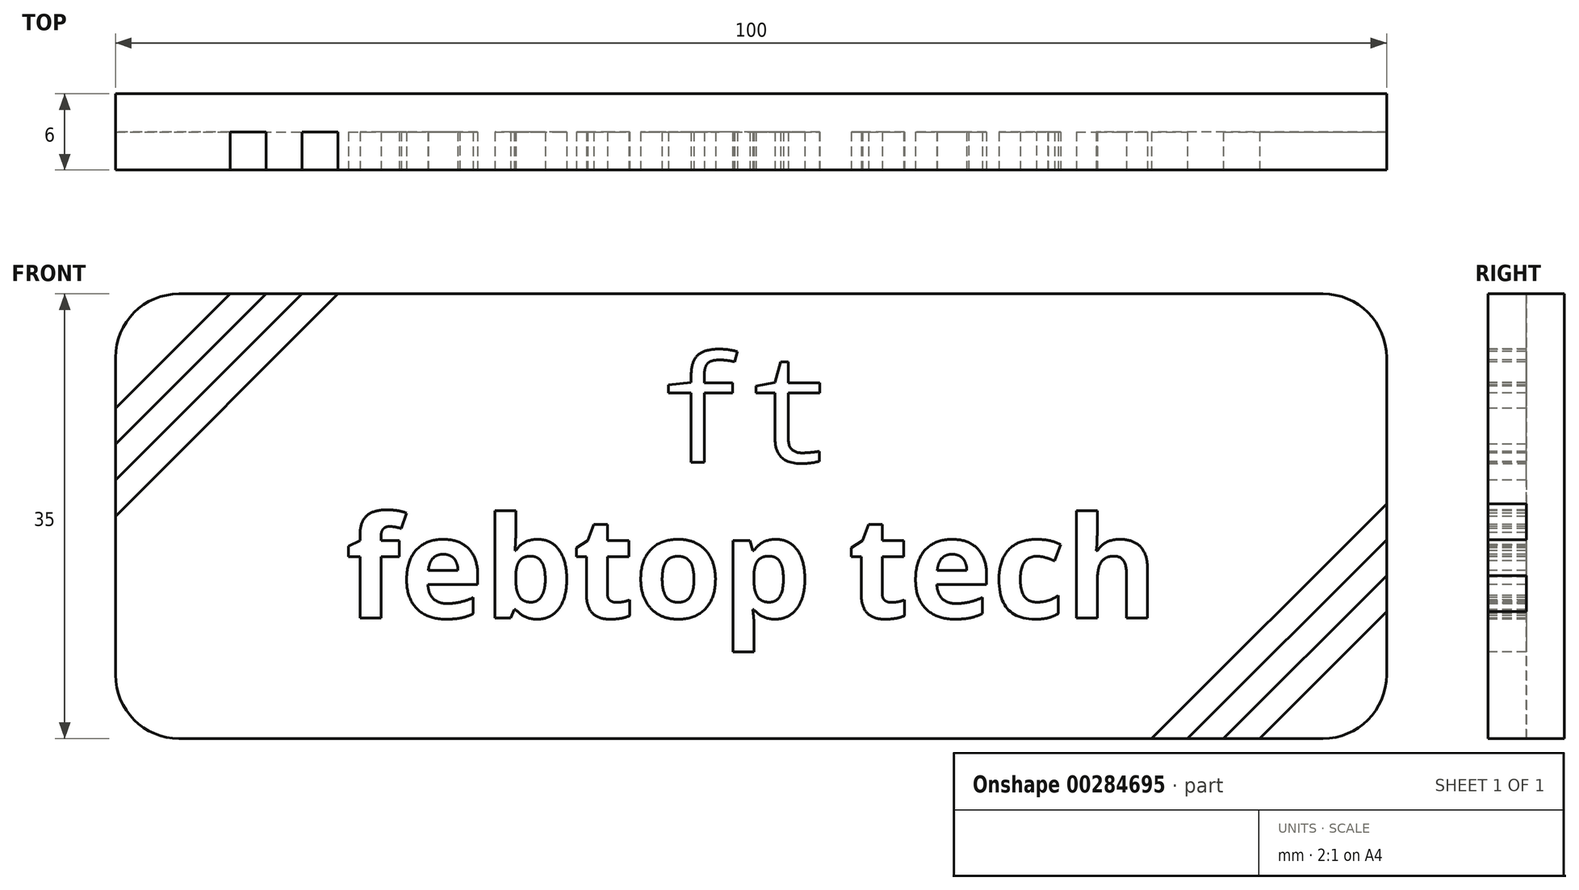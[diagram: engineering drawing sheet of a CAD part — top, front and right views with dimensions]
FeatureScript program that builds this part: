
annotation { "Feature Type Name" : "Feature", "Feature Type Description" : "" }
export const myFeature = defineFeature(function(context is Context, id is Id, definition is map)
    precondition{}
    {
        {
            var Q0;
            Q0=qCreatedBy(makeId("Front.planeOp"),FACE);
            var sketch = newSketch(context, id + "F0", { "sketchPlane" : qUnion([Q0])});
            skLineSegment(sketch, "E0.bottom", {"start": v(-45, 17.5) * mm, "end": v(45, 17.5) * mm});
            skLineSegment(sketch, "E0.top", {"start": v(-45, -17.5) * mm, "end": v(45, -17.5) * mm});
            skLineSegment(sketch, "E0.left", {"start": v(-50, 12.5) * mm, "end": v(-50, -12.5) * mm});
            skLineSegment(sketch, "E0.right", {"start": v(50, 12.5) * mm, "end": v(50, -12.5) * mm});
            skPoint(sketch, "E1.visualSharp", {"position": v(-50, 17.5) * mm});
            skArc(sketch, "E1.filletArc", {"start": v(-45, 17.5) * mm, "mid": v(-48.54, 16.04) * mm, "end": v(-50, 12.5) * mm});
            skPoint(sketch, "E2.visualSharp", {"position": v(-50, -17.5) * mm});
            skArc(sketch, "E2.filletArc", {"start": v(-50, -12.5) * mm, "mid": v(-48.54, -16.04) * mm, "end": v(-45, -17.5) * mm});
            skPoint(sketch, "E3.visualSharp", {"position": v(50, -17.5) * mm});
            skArc(sketch, "E3.filletArc", {"start": v(45, -17.5) * mm, "mid": v(48.54, -16.04) * mm, "end": v(50, -12.5) * mm});
            skPoint(sketch, "E4.visualSharp", {"position": v(50, 17.5) * mm});
            skArc(sketch, "E4.filletArc", {"start": v(50, 12.5) * mm, "mid": v(48.54, 16.04) * mm, "end": v(45, 17.5) * mm});
            skSolve(sketch);
        }
        {
            var Q0;
            Q0=makeQuery(id+"F0.imprint","IMPRINT",FACE,{"disambiguationData":[TD([[makeQuery(id+"F0.imprint","IMPRINT",EDGE,{"derivedFrom":sQuery(id+"F0.wireOp",EDGE,"E0.bottom")}),-1.0]])]});
            extrude(context, id + "F1", {"entities" : qUnion([Q0]), "depth" : 6 * mm});
        }
        {
            var Q0;
            Q0=makeQuery(id+"F1.opExtrude","CAP_FACE",FACE,{"disambiguationData":[OSD([sQuery(id+"F0.wireOp",EDGE,"E0.bottom"),sQuery(id+"F0.wireOp",EDGE,"E0.top"),sQuery(id+"F0.wireOp",EDGE,"E0.left"),sQuery(id+"F0.wireOp",EDGE,"E0.right"),sQuery(id+"F0.wireOp",EDGE,"E1.filletArc"),sQuery(id+"F0.wireOp",EDGE,"E2.filletArc"),sQuery(id+"F0.wireOp",EDGE,"E3.filletArc"),sQuery(id+"F0.wireOp",EDGE,"E4.filletArc")])],"isStart":false});
            var sketch = newSketch(context, id + "F2", { "sketchPlane" : qUnion([Q0])});
            skLineSegment(sketch, "E5", {"start": v(-40.99, 17.5) * mm, "end": v(-50, 8.49) * mm});
            skLineSegment(sketch, "E6", {"start": v(-50, 8.49) * mm, "end": v(-50, 5.66) * mm});
            skLineSegment(sketch, "E7", {"start": v(-50, 5.66) * mm, "end": v(-38.16, 17.5) * mm});
            skLineSegment(sketch, "E8", {"start": v(-50, 2.83) * mm, "end": v(-35.33, 17.5) * mm});
            skLineSegment(sketch, "E9", {"start": v(-50, 0) * mm, "end": v(-32.5, 17.5) * mm});
            skLineSegment(sketch, "E10", {"start": v(40, -17.5) * mm, "end": v(50, -7.5) * mm});
            skLineSegment(sketch, "E11", {"start": v(37.17, -17.5) * mm, "end": v(50, -4.67) * mm});
            skLineSegment(sketch, "E12", {"start": v(50, -1.84) * mm, "end": v(34.34, -17.5) * mm});
            skLineSegment(sketch, "E13", {"start": v(50, 0.99) * mm, "end": v(31.51, -17.5) * mm});
            skSolve(sketch);
        }
        {
            var Q0;
            {var subQ0=sQuery(id+"F2.wireOp",EDGE,"E5");Q0=makeQuery(id+"F2.imprint","IMPRINT",FACE,{"disambiguationData":[TD([[makeQuery(id+"F2.imprint","IMPRINT",EDGE,{"derivedFrom":subQ0}),1.0]])]});}
            var Q1;
            {var subQ0=sQuery(id+"F2.wireOp",EDGE,"E8");Q1=makeQuery(id+"F2.imprint","IMPRINT",FACE,{"disambiguationData":[TD([[makeQuery(id+"F2.imprint","IMPRINT",EDGE,{"derivedFrom":subQ0}),-1.0]])]});}
            var Q2;
            {var subQ0=sQuery(id+"F2.wireOp",EDGE,"E12");Q2=makeQuery(id+"F2.imprint","IMPRINT",FACE,{"disambiguationData":[TD([[makeQuery(id+"F2.imprint","IMPRINT",EDGE,{"derivedFrom":subQ0}),-1.0]])]});}
            var Q3;
            {var subQ0=sQuery(id+"F2.wireOp",EDGE,"E10");Q3=makeQuery(id+"F2.imprint","IMPRINT",FACE,{"disambiguationData":[TD([[makeQuery(id+"F2.imprint","IMPRINT",EDGE,{"derivedFrom":subQ0}),1.0]])]});}
            extrude(context, id + "F3", {"entities" : qUnion([Q0, Q1, Q2, Q3]), "operationType" : NewBodyOperationType.REMOVE, "oppositeDirection" : true, "depth" : 3 * mm});
        }
        {
            var Q0;
            {var subQ0=sQuery(id+"F0.wireOp",EDGE,"E0.left");var subQ1=sQuery(id+"F0.wireOp",EDGE,"E0.top");var subQ2=sQuery(id+"F0.wireOp",EDGE,"E0.right");var subQ3=sQuery(id+"F0.wireOp",EDGE,"E0.bottom");var subQ4=sQuery(id+"F0.wireOp",EDGE,"E2.filletArc");var subQ5=sQuery(id+"F0.wireOp",EDGE,"E4.filletArc");Q0=makeQuery(id+"F3.boolean.opBoolean","SPLIT",FACE,{"disambiguationData":[TD([makeQuery(id+"F1.opExtrude","SWEPT_FACE",FACE,{"disambiguationData":[OSD([subQ4])]})])],"derivedFrom":makeQuery(id+"F1.opExtrude","CAP_FACE",FACE,{"disambiguationData":[OSD([subQ3,subQ1,subQ0,subQ2,sQuery(id+"F0.wireOp",EDGE,"E1.filletArc"),subQ4,sQuery(id+"F0.wireOp",EDGE,"E3.filletArc"),subQ5])],"isStart":false})});}
            var sketch = newSketch(context, id + "F4", { "sketchPlane" : qUnion([Q0])});
            skText(sketch, "E14", { "text": "febtop tech", "fontName": "OpenSans-Bold.ttf"});
            skText(sketch, "E15", { "text": "ft", "fontName": "DroidSansMono.ttf"});
            const initialGuessF4  = {"E14": [-0.0319, -0.008, 1, 0, 0.008], "E15": [-0.0074, 0.00425, 1, 0, 0.00838]};
            skSetInitialGuess(sketch, initialGuessF4);
            skSolve(sketch);
        }
        {
            var Q0;
            Q0=makeQuery(id+"F4.imprint","IMPRINT",FACE,{"disambiguationData":[TD([[makeQuery(id+"F4.imprint","IMPRINT",EDGE,{"derivedFrom":sQuery(id+"F4.wireOp",EDGE,"E14.sketch_text.stroke-0")}),-1.0]])]});
            var Q1;
            Q1=makeQuery(id+"F4.imprint","IMPRINT",FACE,{"disambiguationData":[TD([[makeQuery(id+"F4.imprint","IMPRINT",EDGE,{"derivedFrom":sQuery(id+"F4.wireOp",EDGE,"E14.sketch_text.stroke-18")}),-1.0]])]});
            var Q2;
            Q2=makeQuery(id+"F4.imprint","IMPRINT",FACE,{"disambiguationData":[TD([[makeQuery(id+"F4.imprint","IMPRINT",EDGE,{"derivedFrom":sQuery(id+"F4.wireOp",EDGE,"E14.sketch_text.stroke-38")}),-1.0]])]});
            var Q3;
            Q3=makeQuery(id+"F4.imprint","IMPRINT",FACE,{"disambiguationData":[TD([[makeQuery(id+"F4.imprint","IMPRINT",EDGE,{"derivedFrom":sQuery(id+"F4.wireOp",EDGE,"E14.sketch_text.stroke-61")}),-1.0]])]});
            var Q4;
            Q4=makeQuery(id+"F4.imprint","IMPRINT",FACE,{"disambiguationData":[TD([[makeQuery(id+"F4.imprint","IMPRINT",EDGE,{"derivedFrom":sQuery(id+"F4.wireOp",EDGE,"E14.sketch_text.stroke-79")}),-1.0]])]});
            var Q5;
            Q5=makeQuery(id+"F4.imprint","IMPRINT",FACE,{"disambiguationData":[TD([[makeQuery(id+"F4.imprint","IMPRINT",EDGE,{"derivedFrom":sQuery(id+"F4.wireOp",EDGE,"E14.sketch_text.stroke-97")}),-1.0]])]});
            var Q6;
            Q6=makeQuery(id+"F4.imprint","IMPRINT",FACE,{"disambiguationData":[TD([[makeQuery(id+"F4.imprint","IMPRINT",EDGE,{"derivedFrom":sQuery(id+"F4.wireOp",EDGE,"E14.sketch_text.stroke-120")}),-1.0]])]});
            var Q7;
            Q7=makeQuery(id+"F4.imprint","IMPRINT",FACE,{"disambiguationData":[TD([[makeQuery(id+"F4.imprint","IMPRINT",EDGE,{"derivedFrom":sQuery(id+"F4.wireOp",EDGE,"E14.sketch_text.stroke-138")}),-1.0]])]});
            var Q8;
            Q8=makeQuery(id+"F4.imprint","IMPRINT",FACE,{"disambiguationData":[TD([[makeQuery(id+"F4.imprint","IMPRINT",EDGE,{"derivedFrom":sQuery(id+"F4.wireOp",EDGE,"E14.sketch_text.stroke-158")}),-1.0]])]});
            var Q9;
            Q9=makeQuery(id+"F4.imprint","IMPRINT",FACE,{"disambiguationData":[TD([[makeQuery(id+"F4.imprint","IMPRINT",EDGE,{"derivedFrom":sQuery(id+"F4.wireOp",EDGE,"E14.sketch_text.stroke-172")}),-1.0]])]});
            var Q10;
            Q10=makeQuery(id+"F4.imprint","IMPRINT",FACE,{"disambiguationData":[TD([[makeQuery(id+"F4.imprint","IMPRINT",EDGE,{"derivedFrom":sQuery(id+"F4.wireOp",EDGE,"E15.sketch_text.stroke-0")}),-1.0]])]});
            var Q11;
            Q11=makeQuery(id+"F4.imprint","IMPRINT",FACE,{"disambiguationData":[TD([[makeQuery(id+"F4.imprint","IMPRINT",EDGE,{"derivedFrom":sQuery(id+"F4.wireOp",EDGE,"E15.sketch_text.stroke-18")}),-1.0]])]});
            extrude(context, id + "F5", {"entities" : qUnion([Q0, Q1, Q2, Q3, Q4, Q5, Q6, Q7, Q8, Q9, Q10, Q11]), "operationType" : NewBodyOperationType.REMOVE, "oppositeDirection" : true, "depth" : 3 * mm});
        }
    });
